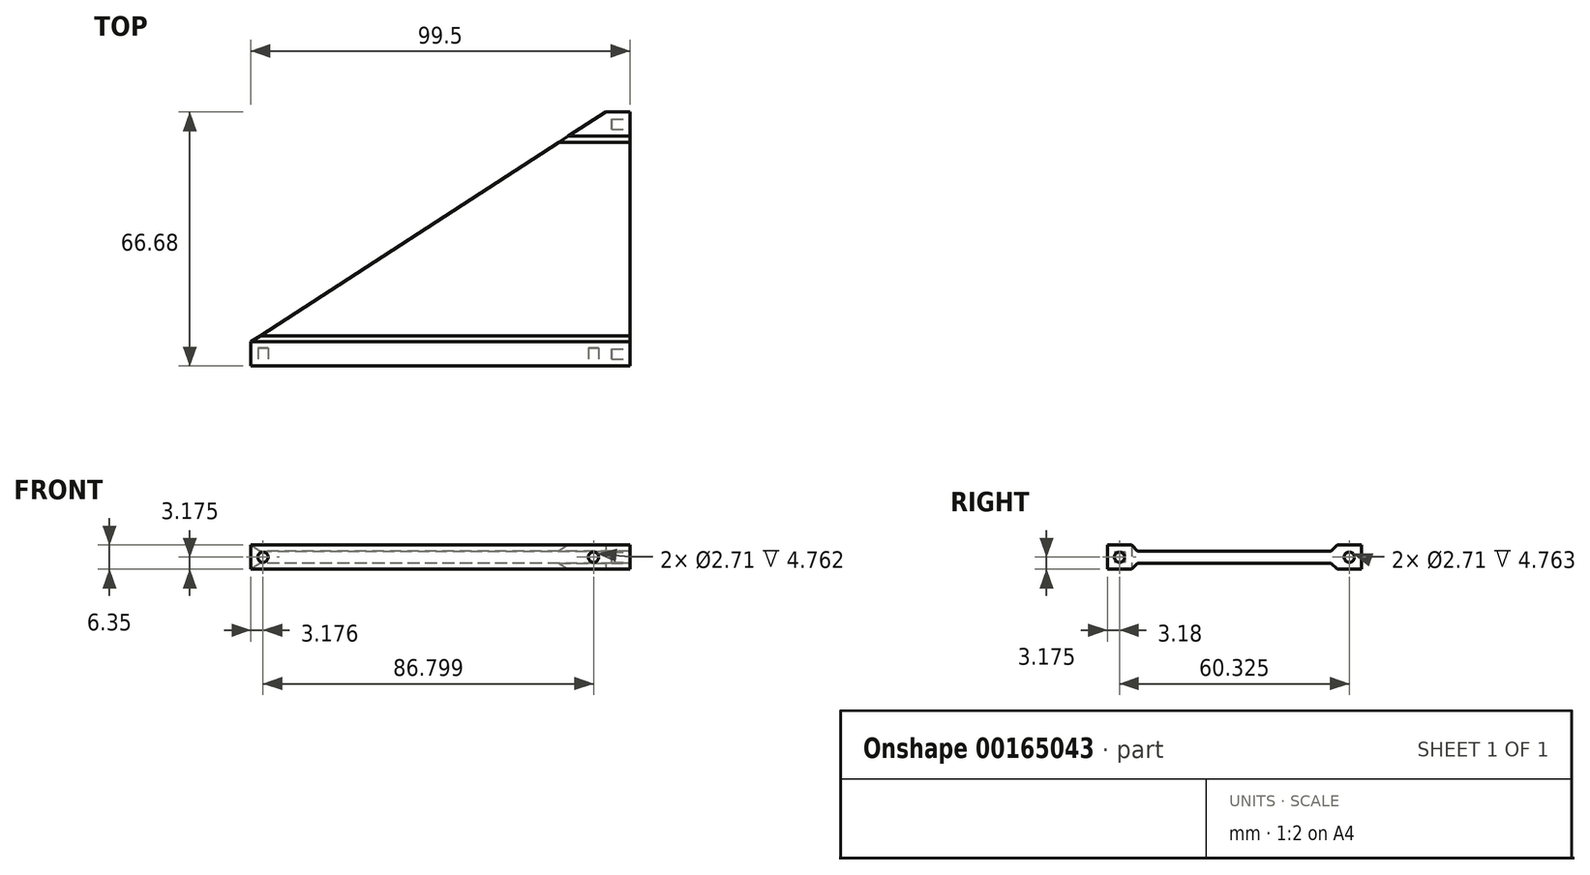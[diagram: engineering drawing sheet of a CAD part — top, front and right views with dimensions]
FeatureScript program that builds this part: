
annotation { "Feature Type Name" : "Feature", "Feature Type Description" : "" }
export const myFeature = defineFeature(function(context is Context, id is Id, definition is map)
    precondition{}
    {
        {
            var Q0;
            Q0=qCreatedBy(makeId("Top.planeOp"),FACE);
            var sketch = newSketch(context, id + "F0", { "sketchPlane" : qUnion([Q0])});
            skLineSegment(sketch, "E0.bottom", {"start": v(0, 0) * mm, "end": v(-6.35, 0) * mm});
            skLineSegment(sketch, "E0.top", {"start": v(0, -66.68) * mm, "end": v(-99.5, -66.68) * mm});
            skLineSegment(sketch, "E0.left", {"start": v(0, 0) * mm, "end": v(0, -66.68) * mm});
            skLineSegment(sketch, "E1", {"start": v(-6.35, 0) * mm, "end": v(-99.5, -60.33) * mm});
            skLineSegment(sketch, "E2", {"start": v(-99.5, -60.33) * mm, "end": v(-99.5, -66.68) * mm});
            skSolve(sketch);
        }
        {
            var Q0;
            Q0 = qSketchRegion(id + "F0", true);
            extrude(context, id + "F1", {"entities" : qUnion([Q0]), "depth" : 6.35 * mm});
        }
        {
            var Q0;
            Q0=makeQuery(id+"F1.opExtrude","SWEPT_FACE",FACE,{"disambiguationData":[OSD([sQuery(id+"F0.wireOp",EDGE,"E0.left")])]});
            var sketch = newSketch(context, id + "F2", { "sketchPlane" : qUnion([Q0])});
            skLineSegment(sketch, "E3.bottom", {"start": v(0, 3.18) * mm, "end": v(-3.17, 3.18) * mm, "construction": true});
            skLineSegment(sketch, "E3.top", {"start": v(0, 6.35) * mm, "end": v(-3.17, 6.35) * mm, "construction": true});
            skLineSegment(sketch, "E3.left", {"start": v(0, 3.18) * mm, "end": v(0, 6.35) * mm, "construction": true});
            skLineSegment(sketch, "E3.right", {"start": v(-3.17, 3.18) * mm, "end": v(-3.17, 6.35) * mm, "construction": true});
            skLineSegment(sketch, "E4.bottom", {"start": v(-66.68, 3.18) * mm, "end": v(-63.5, 3.18) * mm, "construction": true});
            skLineSegment(sketch, "E4.top", {"start": v(-66.68, 0) * mm, "end": v(-63.5, 0) * mm, "construction": true});
            skLineSegment(sketch, "E4.left", {"start": v(-66.68, 3.17) * mm, "end": v(-66.68, 0) * mm, "construction": true});
            skLineSegment(sketch, "E4.right", {"start": v(-63.5, 3.17) * mm, "end": v(-63.5, 0) * mm, "construction": true});
            skCircle(sketch, "E5", {"center": v(-63.5, 3.17) * mm, "radius": 1.35 * mm});
            skCircle(sketch, "E6", {"center": v(-3.17, 3.18) * mm, "radius": 1.35 * mm});
            skSolve(sketch);
        }
        {
            var Q0;
            Q0 = qSketchRegion(id + "F2", true);
            extrude(context, id + "F3", {"entities" : qUnion([Q0]), "operationType" : NewBodyOperationType.REMOVE, "oppositeDirection" : true, "depth" : 4.76 * mm});
        }
        {
            var Q0;
            Q0=makeQuery(id+"F1.opExtrude","SWEPT_FACE",FACE,{"disambiguationData":[OSD([sQuery(id+"F0.wireOp",EDGE,"E0.top")])]});
            var sketch = newSketch(context, id + "F4", { "sketchPlane" : qUnion([Q0])});
            skLineSegment(sketch, "E7.bottom", {"start": v(-99.5, 3.18) * mm, "end": v(-96.32, 3.18) * mm, "construction": true});
            skLineSegment(sketch, "E7.top", {"start": v(-99.5, 0) * mm, "end": v(-96.32, 0) * mm, "construction": true});
            skLineSegment(sketch, "E7.left", {"start": v(-99.5, 3.18) * mm, "end": v(-99.5, 0) * mm, "construction": true});
            skLineSegment(sketch, "E7.right", {"start": v(-96.32, 3.18) * mm, "end": v(-96.32, 0) * mm, "construction": true});
            skLineSegment(sketch, "E8.bottom", {"start": v(0, 3.18) * mm, "end": v(-9.53, 3.18) * mm, "construction": true});
            skLineSegment(sketch, "E8.top", {"start": v(0, 0) * mm, "end": v(-9.53, 0) * mm, "construction": true});
            skLineSegment(sketch, "E8.left", {"start": v(0, 3.18) * mm, "end": v(0, 0) * mm, "construction": true});
            skLineSegment(sketch, "E8.right", {"start": v(-9.53, 3.18) * mm, "end": v(-9.53, 0) * mm, "construction": true});
            skCircle(sketch, "E9", {"center": v(-96.32, 3.18) * mm, "radius": 1.35 * mm});
            skCircle(sketch, "E10", {"center": v(-9.53, 3.18) * mm, "radius": 1.35 * mm});
            skSolve(sketch);
        }
        {
            var Q0;
            Q0 = qSketchRegion(id + "F4", true);
            extrude(context, id + "F5", {"entities" : qUnion([Q0]), "operationType" : NewBodyOperationType.REMOVE, "oppositeDirection" : true, "depth" : 4.76 * mm});
        }
        {
            var Q0;
            Q0=makeQuery(id+"F1.opExtrude","SWEPT_FACE",FACE,{"disambiguationData":[OSD([sQuery(id+"F0.wireOp",EDGE,"E0.left")])]});
            var sketch = newSketch(context, id + "F6", { "sketchPlane" : qUnion([Q0])});
            skLineSegment(sketch, "E11.bottom", {"start": v(-6.35, 6.35) * mm, "end": v(-60.32, 6.35) * mm});
            skLineSegment(sketch, "E11.top", {"start": v(-6.35, 4.76) * mm, "end": v(-60.32, 4.76) * mm});
            skLineSegment(sketch, "E11.left", {"start": v(-6.35, 6.35) * mm, "end": v(-6.35, 4.76) * mm});
            skLineSegment(sketch, "E11.right", {"start": v(-60.32, 6.35) * mm, "end": v(-60.32, 4.76) * mm});
            skLineSegment(sketch, "E12.bottom", {"start": v(-6.35, 0) * mm, "end": v(-60.32, 0) * mm});
            skLineSegment(sketch, "E12.top", {"start": v(-6.35, 1.59) * mm, "end": v(-60.32, 1.59) * mm});
            skLineSegment(sketch, "E12.left", {"start": v(-6.35, 0) * mm, "end": v(-6.35, 1.59) * mm});
            skLineSegment(sketch, "E12.right", {"start": v(-60.32, 0) * mm, "end": v(-60.32, 1.59) * mm});
            skLineSegment(sketch, "E13", {"start": v(-6.35, 4.76) * mm, "end": v(-6.35, 1.59) * mm, "construction": true});
            skLineSegment(sketch, "E14", {"start": v(-60.32, 4.76) * mm, "end": v(-60.32, 1.59) * mm, "construction": true});
            skLineSegment(sketch, "E15", {"start": v(-6.35, 3.18) * mm, "end": v(-3.17, 3.18) * mm, "construction": true});
            skLineSegment(sketch, "E16", {"start": v(-66.68, 3.18) * mm, "end": v(-63.5, 3.18) * mm, "construction": true});
            skLineSegment(sketch, "E17", {"start": v(-63.5, 3.17) * mm, "end": v(-60.32, 3.17) * mm, "construction": true});
            skSolve(sketch);
        }
        {
            var Q0;
            Q0 = qSketchRegion(id + "F6", true);
            extrude(context, id + "F7", {"entities" : qUnion([Q0]), "operationType" : NewBodyOperationType.REMOVE, "endBound" : BoundingType.THROUGH_ALL, "oppositeDirection" : true, "depth" : 25.4 * mm});
        }
        {
            var Q0;
            Q0=makeQuery(id+"F7.boolean.opBoolean","COPY",EDGE,{"derivedFrom":makeQuery(id+"F7.opExtrude","SWEPT_EDGE",EDGE,{"disambiguationData":[OSD([sQuery(id+"F6.wireOp",EDGE,"E11.top"),sQuery(id+"F6.wireOp",EDGE,"E11.right")])]})});
            var Q1;
            Q1=makeQuery(id+"F7.boolean.opBoolean","COPY",EDGE,{"derivedFrom":makeQuery(id+"F7.opExtrude","SWEPT_EDGE",EDGE,{"disambiguationData":[OSD([sQuery(id+"F6.wireOp",EDGE,"E12.top"),sQuery(id+"F6.wireOp",EDGE,"E12.right")])]})});
            var Q2;
            Q2=makeQuery(id+"F7.boolean.opBoolean","COPY",EDGE,{"derivedFrom":makeQuery(id+"F7.opExtrude","SWEPT_EDGE",EDGE,{"disambiguationData":[OSD([sQuery(id+"F6.wireOp",EDGE,"E11.top"),sQuery(id+"F6.wireOp",EDGE,"E11.left")])]})});
            var Q3;
            Q3=makeQuery(id+"F7.boolean.opBoolean","COPY",EDGE,{"derivedFrom":makeQuery(id+"F7.opExtrude","SWEPT_EDGE",EDGE,{"disambiguationData":[OSD([sQuery(id+"F6.wireOp",EDGE,"E12.top"),sQuery(id+"F6.wireOp",EDGE,"E12.left")])]})});
            chamfer(context, id + "F8", {"entities" : qUnion([Q0, Q1, Q2, Q3]), "width" : 1.59 * mm, "tangentPropagation" : true});
        }
    });
